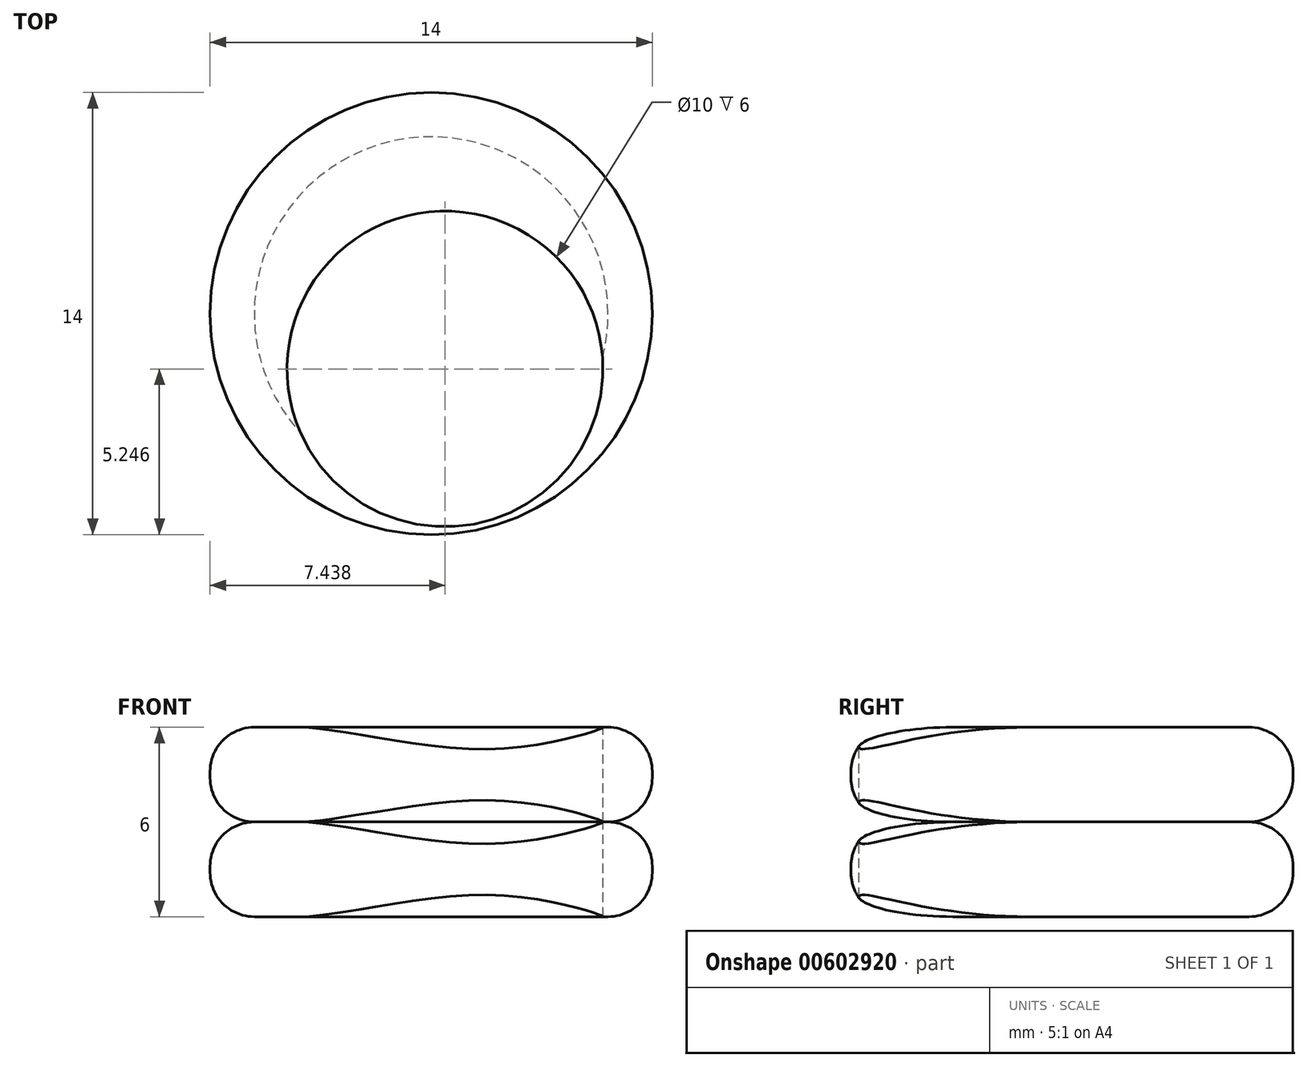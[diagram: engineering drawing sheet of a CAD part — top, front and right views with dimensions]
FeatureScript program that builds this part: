
annotation { "Feature Type Name" : "Feature", "Feature Type Description" : "" }
export const myFeature = defineFeature(function(context is Context, id is Id, definition is map)
    precondition{}
    {
        {
            var Q0;
            Q0=qCreatedBy(makeId("Top.planeOp"),FACE);
            var sketch = newSketch(context, id + "F0", { "sketchPlane" : qUnion([Q0])});
            skCircle(sketch, "E0", {"center": v(0, 0) * mm, "radius": 7 * mm});
            skSolve(sketch);
        }
        {
            var Q0;
            Q0=makeQuery(id+"F0.imprint","IMPRINT",FACE,{"disambiguationData":[TD([[makeQuery(id+"F0.imprint","IMPRINT",EDGE,{"derivedFrom":sQuery(id+"F0.wireOp",EDGE,"E0")}),1.0]])]});
            extrude(context, id + "F1", {"entities" : qUnion([Q0]), "depth" : 3 * mm, "offsetDistance" : 25 * mm});
        }
        {
            var Q0;
            Q0=makeQuery(id+"F1.opExtrude","CAP_EDGE",EDGE,{"disambiguationData":[OSD([sQuery(id+"F0.wireOp",EDGE,"E0")])],"isStart":false});
            var Q1;
            Q1=makeQuery(id+"F1.opExtrude","CAP_EDGE",EDGE,{"disambiguationData":[OSD([sQuery(id+"F0.wireOp",EDGE,"E0")])],"isStart":true});
            fillet(context, id + "F2", {"entities" : qUnion([Q0, Q1]), "radius" : 1.4 * mm, "tangentPropagation" : true, "allowEdgeOverflow" : false});
        }
        {
            var Q0;
            Q0=makeQuery(id+"F1.opExtrude","CAP_FACE",FACE,{"disambiguationData":[OSD([sQuery(id+"F0.wireOp",EDGE,"E0")])],"isStart":false});
            var sketch = newSketch(context, id + "F3", { "sketchPlane" : qUnion([Q0])});
            skCircle(sketch, "E1", {"center": v(0, 0) * mm, "radius": 7 * mm});
            skSolve(sketch);
        }
        {
            var Q0;
            Q0=makeQuery(id+"F3.imprint","IMPRINT",FACE,{"disambiguationData":[TD([[makeQuery(id+"F3.imprint","IMPRINT",EDGE,{"derivedFrom":sQuery(id+"F3.wireOp",EDGE,"E1")}),1.0]])]});
            var Q1;
            {var subQ0=sQuery(id+"F0.wireOp",EDGE,"E0");Q1=makeQuery(id+"F3.imprint","IMPRINT",FACE,{"disambiguationData":[TD([[makeQuery(id+"F3.imprint","IMPRINT",EDGE,{"derivedFrom":makeQuery(id+"F2.opFillet","BLEND_EDGE",EDGE,{"blendedFrom":[makeQuery(id+"F1.opExtrude","CAP_EDGE",EDGE,{"disambiguationData":[OSD([subQ0])],"isStart":false}),makeQuery(id+"F1.opExtrude","CAP_FACE",FACE,{"disambiguationData":[OSD([subQ0])],"isStart":false})],"blendedInto":[makeQuery(id+"F1.opExtrude","CAP_FACE",FACE,{"disambiguationData":[OSD([subQ0])],"isStart":false})]})}),1.0]])]});}
            extrude(context, id + "F4", {"entities" : qUnion([Q0, Q1]), "operationType" : NewBodyOperationType.ADD, "depth" : 3 * mm, "offsetDistance" : 25 * mm});
        }
        {
            var Q0;
            Q0=makeQuery(id+"F4.opExtrude","CAP_EDGE",EDGE,{"disambiguationData":[OSD([sQuery(id+"F3.wireOp",EDGE,"E1")])],"isStart":true});
            var Q1;
            Q1=makeQuery(id+"F4.opExtrude","CAP_EDGE",EDGE,{"disambiguationData":[OSD([sQuery(id+"F3.wireOp",EDGE,"E1")])],"isStart":false});
            fillet(context, id + "F5", {"entities" : qUnion([Q0, Q1]), "radius" : 1.4 * mm, "tangentPropagation" : true, "allowEdgeOverflow" : false});
        }
        {
            var Q0;
            Q0=makeQuery(id+"F4.opExtrude","CAP_FACE",FACE,{"disambiguationData":[OSD([sQuery(id+"F3.wireOp",EDGE,"E1")])],"isStart":false});
            var sketch = newSketch(context, id + "F6", { "sketchPlane" : qUnion([Q0])});
            skPoint(sketch, "E2", {"position": v(0.44, -1.75) * mm});
            skSolve(sketch);
        }
        {
            var Q0;
            Q0=sQuery(id+"F6.wireOp",VERTEX,"E2");
            var Q1;
            Q1=makeQuery(id+"F1.opExtrude","SWEPT_BODY",BODY,{"disambiguationData":[OSD([sQuery(id+"F0.wireOp",EDGE,"E0")])]});
            hole(context, id + "F7", {"style" : HoleStyle.SIMPLE, "endStyle" : HoleEndStyle.THROUGH, "holeDiameter" : 10 * mm, "majorDiameter" : 5 * mm, "isTappedThrough" : true, "tappedDepth" : 12 * mm, "tapClearance" : 3, "locations" : qUnion([Q0]), "scope" : qUnion([Q1])});
        }
    });
